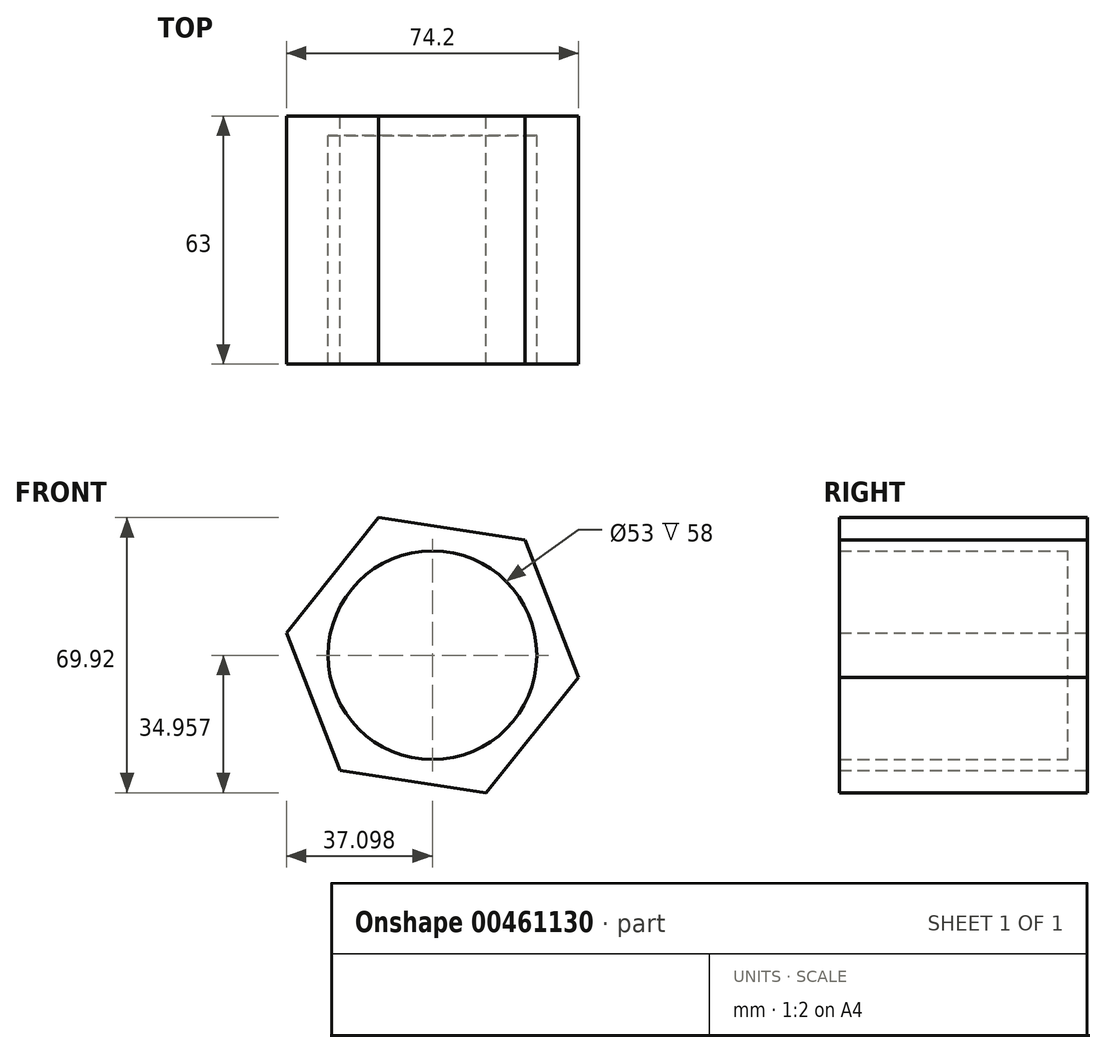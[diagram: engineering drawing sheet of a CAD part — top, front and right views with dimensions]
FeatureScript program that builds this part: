
annotation { "Feature Type Name" : "Feature", "Feature Type Description" : "" }
export const myFeature = defineFeature(function(context is Context, id is Id, definition is map)
    precondition{}
    {
        {
            var Q0;
            Q0=qCreatedBy(makeId("Front.planeOp"),FACE);
            var sketch = newSketch(context, id + "F0", { "sketchPlane" : qUnion([Q0])});
            skCircle(sketch, "E0.cCircle", {"center": v(-9.9, -5) * mm, "radius": 32.5 * mm, "construction": true});
            skLineSegment(sketch, "E0.0", {"start": v(27.2, -10.66) * mm, "end": v(3.74, -39.95) * mm});
            skLineSegment(sketch, "E0.1", {"start": v(3.74, -39.95) * mm, "end": v(-33.35, -34.3) * mm});
            skLineSegment(sketch, "E0.2", {"start": v(-33.35, -34.3) * mm, "end": v(-47, 0.67) * mm});
            skLineSegment(sketch, "E0.3", {"start": v(-47, 0.67) * mm, "end": v(-23.55, 29.97) * mm});
            skLineSegment(sketch, "E0.4", {"start": v(-23.55, 29.97) * mm, "end": v(13.55, 24.3) * mm});
            skLineSegment(sketch, "E0.5", {"start": v(13.55, 24.3) * mm, "end": v(27.2, -10.66) * mm});
            skPoint(sketch, "E0.0.midPoint", {"position": v(15.47, -25.3) * mm});
            skCircle(sketch, "E1", {"center": v(-9.9, -5) * mm, "radius": 26.5 * mm});
            skSolve(sketch);
        }
        {
            var Q0;
            Q0 = qSketchRegion(id + "F0", true);
            extrude(context, id + "F1", {"entities" : qUnion([Q0]), "depth" : 58 * mm});
        }
        {
            var Q0;
            Q0=makeQuery(id+"F1.opExtrude","CAP_FACE",FACE,{"disambiguationData":[OSD([sQuery(id+"F0.wireOp",EDGE,"E0.0"),sQuery(id+"F0.wireOp",EDGE,"E0.1"),sQuery(id+"F0.wireOp",EDGE,"E0.2"),sQuery(id+"F0.wireOp",EDGE,"E0.3"),sQuery(id+"F0.wireOp",EDGE,"E0.4"),sQuery(id+"F0.wireOp",EDGE,"E0.5"),sQuery(id+"F0.wireOp",EDGE,"E1")])],"isStart":true});
            var sketch = newSketch(context, id + "F2", { "sketchPlane" : qUnion([Q0])});
            skLineSegment(sketch, "E2.0.0", {"start": v(-13.55, 24.3) * mm, "end": v(-27.2, -10.66) * mm});
            skLineSegment(sketch, "E2.0.1", {"start": v(-27.2, -10.66) * mm, "end": v(-3.74, -39.95) * mm});
            skLineSegment(sketch, "E2.0.2", {"start": v(-3.74, -39.95) * mm, "end": v(33.35, -34.3) * mm});
            skLineSegment(sketch, "E2.0.3", {"start": v(33.35, -34.3) * mm, "end": v(47, 0.67) * mm});
            skLineSegment(sketch, "E2.0.4", {"start": v(47, 0.67) * mm, "end": v(23.55, 29.97) * mm});
            skLineSegment(sketch, "E2.0.5", {"start": v(23.55, 29.97) * mm, "end": v(-13.55, 24.3) * mm});
            skSolve(sketch);
        }
        {
            var Q0;
            Q0 = qSketchRegion(id + "F2", true);
            extrude(context, id + "F3", {"entities" : qUnion([Q0]), "operationType" : NewBodyOperationType.ADD, "depth" : 5 * mm});
        }
    });
